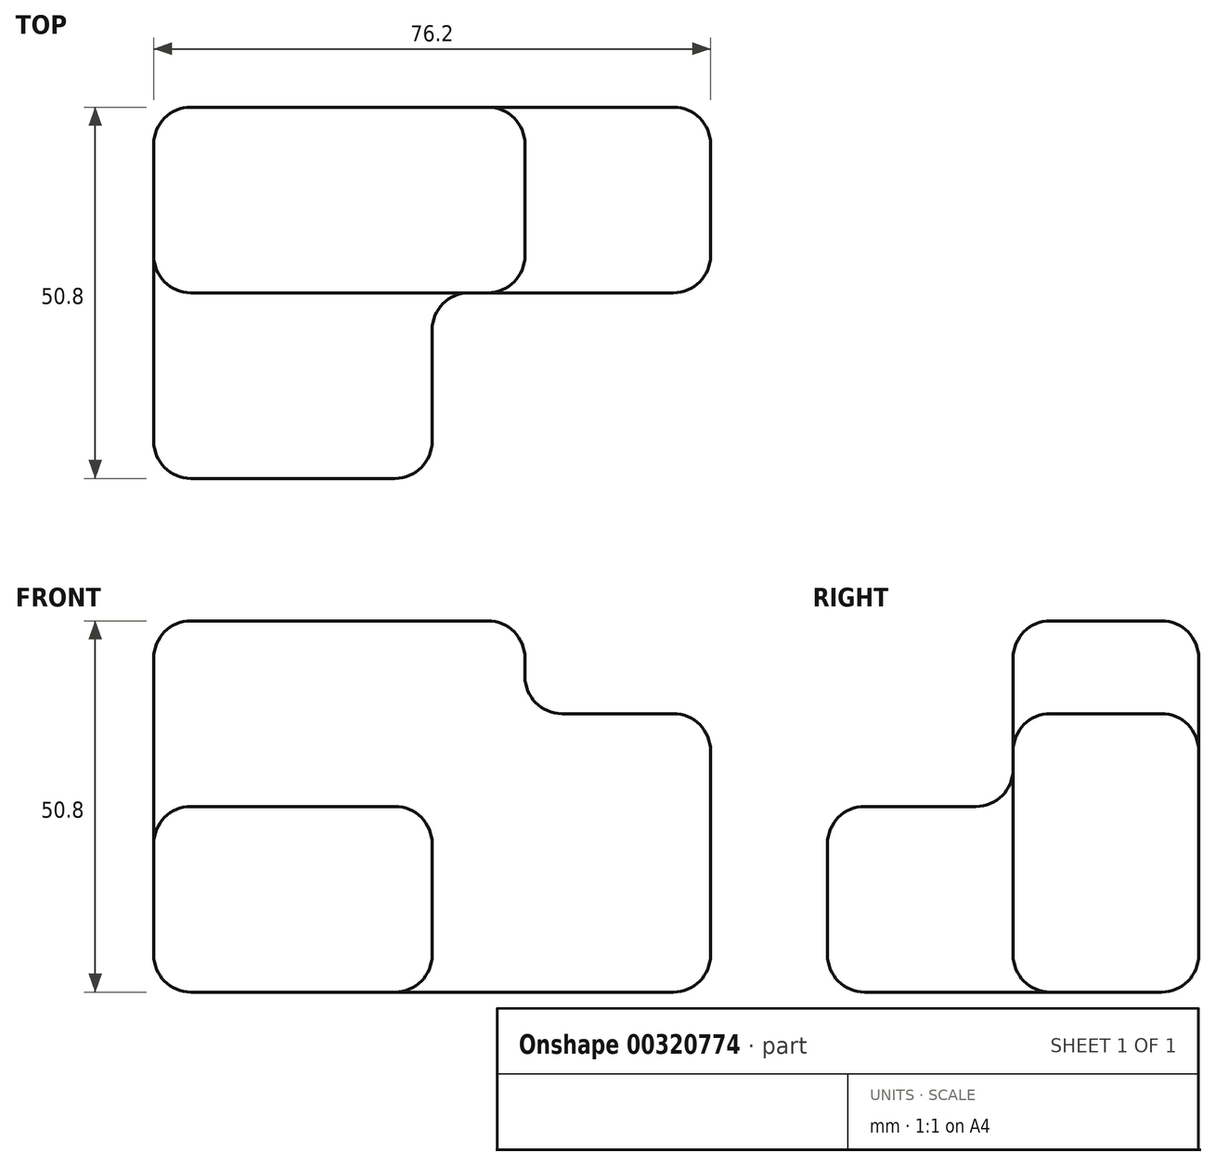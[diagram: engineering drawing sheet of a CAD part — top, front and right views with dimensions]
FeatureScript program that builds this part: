
annotation { "Feature Type Name" : "Feature", "Feature Type Description" : "" }
export const myFeature = defineFeature(function(context is Context, id is Id, definition is map)
    precondition{}
    {
        {
            var Q0;
            Q0=qCreatedBy(makeId("Front.planeOp"),FACE);
            var sketch = newSketch(context, id + "F0", { "sketchPlane" : qUnion([Q0])});
            skLineSegment(sketch, "E0", {"start": v(-44.3, 20) * mm, "end": v(6.5, 20) * mm});
            skLineSegment(sketch, "E1", {"start": v(6.5, 20) * mm, "end": v(6.5, 7.3) * mm});
            skLineSegment(sketch, "E2", {"start": v(6.5, 7.3) * mm, "end": v(31.9, 7.3) * mm});
            skLineSegment(sketch, "E3", {"start": v(31.9, 7.3) * mm, "end": v(31.9, -30.8) * mm});
            skLineSegment(sketch, "E4", {"start": v(31.9, -30.8) * mm, "end": v(-44.3, -30.8) * mm});
            skLineSegment(sketch, "E5", {"start": v(-44.3, -30.8) * mm, "end": v(-44.3, 20) * mm});
            skSolve(sketch);
        }
        {
            var Q0;
            Q0=makeQuery(id+"F0.imprint","IMPRINT",FACE,{"disambiguationData":[TD([[makeQuery(id+"F0.imprint","IMPRINT",EDGE,{"derivedFrom":sQuery(id+"F0.wireOp",EDGE,"E0")}),-1.0]])]});
            extrude(context, id + "F1", {"entities" : qUnion([Q0]), "depth" : 25.4 * mm});
        }
        {
            var Q0;
            Q0=makeQuery(id+"F1.opExtrude","CAP_FACE",FACE,{"disambiguationData":[OSD([sQuery(id+"F0.wireOp",EDGE,"E0"),sQuery(id+"F0.wireOp",EDGE,"E1"),sQuery(id+"F0.wireOp",EDGE,"E2"),sQuery(id+"F0.wireOp",EDGE,"E3"),sQuery(id+"F0.wireOp",EDGE,"E4"),sQuery(id+"F0.wireOp",EDGE,"E5")])],"isStart":false});
            var sketch = newSketch(context, id + "F2", { "sketchPlane" : qUnion([Q0])});
            skLineSegment(sketch, "E6", {"start": v(-44.3, -5.4) * mm, "end": v(-6.2, -5.4) * mm});
            skLineSegment(sketch, "E7", {"start": v(-6.2, -5.4) * mm, "end": v(-6.2, -30.8) * mm});
            skLineSegment(sketch, "E8", {"start": v(-44.3, -5.4) * mm, "end": v(-44.3, -30.8) * mm});
            skLineSegment(sketch, "E9", {"start": v(-44.3, -30.8) * mm, "end": v(-6.2, -30.8) * mm});
            skSolve(sketch);
        }
        {
            var Q0;
            Q0=makeQuery(id+"F2.imprint","IMPRINT",FACE,{"disambiguationData":[TD([[makeQuery(id+"F2.imprint","IMPRINT",EDGE,{"derivedFrom":sQuery(id+"F2.wireOp",EDGE,"E6")}),-1.0]])]});
            extrude(context, id + "F3", {"entities" : qUnion([Q0]), "operationType" : NewBodyOperationType.ADD, "depth" : 25.4 * mm});
        }
        {
            var Q0;
            Q0=makeQuery(id+"F1.opExtrude","SWEPT_FACE",FACE,{"disambiguationData":[OSD([sQuery(id+"F0.wireOp",EDGE,"E0")])]});
            var Q1;
            Q1=makeQuery(id+"F1.opExtrude","SWEPT_FACE",FACE,{"disambiguationData":[OSD([sQuery(id+"F0.wireOp",EDGE,"E2")])]});
            var Q2;
            Q2=makeQuery(id+"F3.opExtrude","CAP_FACE",FACE,{"disambiguationData":[OSD([sQuery(id+"F2.wireOp",EDGE,"E6"),sQuery(id+"F2.wireOp",EDGE,"E7"),sQuery(id+"F2.wireOp",EDGE,"E8"),sQuery(id+"F2.wireOp",EDGE,"E9")])],"isStart":false});
            var Q3;
            Q3=makeQuery(id+"F3.opExtrude","SWEPT_FACE",FACE,{"disambiguationData":[OSD([sQuery(id+"F2.wireOp",EDGE,"E6")])]});
            var Q4;
            Q4=makeQuery(id+"F3.opExtrude","SWEPT_FACE",FACE,{"disambiguationData":[OSD([sQuery(id+"F2.wireOp",EDGE,"E7")])]});
            var Q5;
            Q5=makeQuery(id+"F1.opExtrude","SWEPT_FACE",FACE,{"disambiguationData":[OSD([sQuery(id+"F0.wireOp",EDGE,"E3")])]});
            var Q6;
            Q6=makeQuery(id+"F1.opExtrude","CAP_FACE",FACE,{"disambiguationData":[OSD([sQuery(id+"F0.wireOp",EDGE,"E0"),sQuery(id+"F0.wireOp",EDGE,"E1"),sQuery(id+"F0.wireOp",EDGE,"E2"),sQuery(id+"F0.wireOp",EDGE,"E3"),sQuery(id+"F0.wireOp",EDGE,"E4"),sQuery(id+"F0.wireOp",EDGE,"E5")])],"isStart":false});
            var Q7;
            Q7=makeQuery(id+"F1.opExtrude","CAP_FACE",FACE,{"disambiguationData":[OSD([sQuery(id+"F0.wireOp",EDGE,"E0"),sQuery(id+"F0.wireOp",EDGE,"E1"),sQuery(id+"F0.wireOp",EDGE,"E2"),sQuery(id+"F0.wireOp",EDGE,"E3"),sQuery(id+"F0.wireOp",EDGE,"E4"),sQuery(id+"F0.wireOp",EDGE,"E5")])],"isStart":true});
            var Q8;
            Q8=makeQuery(id+"F3.boolean.opBoolean","MERGE",FACE,{"derivedFrom":[makeQuery(id+"F1.opExtrude","SWEPT_FACE",FACE,{"disambiguationData":[OSD([sQuery(id+"F0.wireOp",EDGE,"E4")])]}),makeQuery(id+"F3.opExtrude","SWEPT_FACE",FACE,{"disambiguationData":[OSD([sQuery(id+"F2.wireOp",EDGE,"E9")])]})]});
            fillet(context, id + "F4", {"entities" : qUnion([Q0, Q1, Q2, Q3, Q4, Q5, Q6, Q7, Q8]), "radius" : 5.08 * mm, "tangentPropagation" : true, "allowEdgeOverflow" : false});
        }
    });
